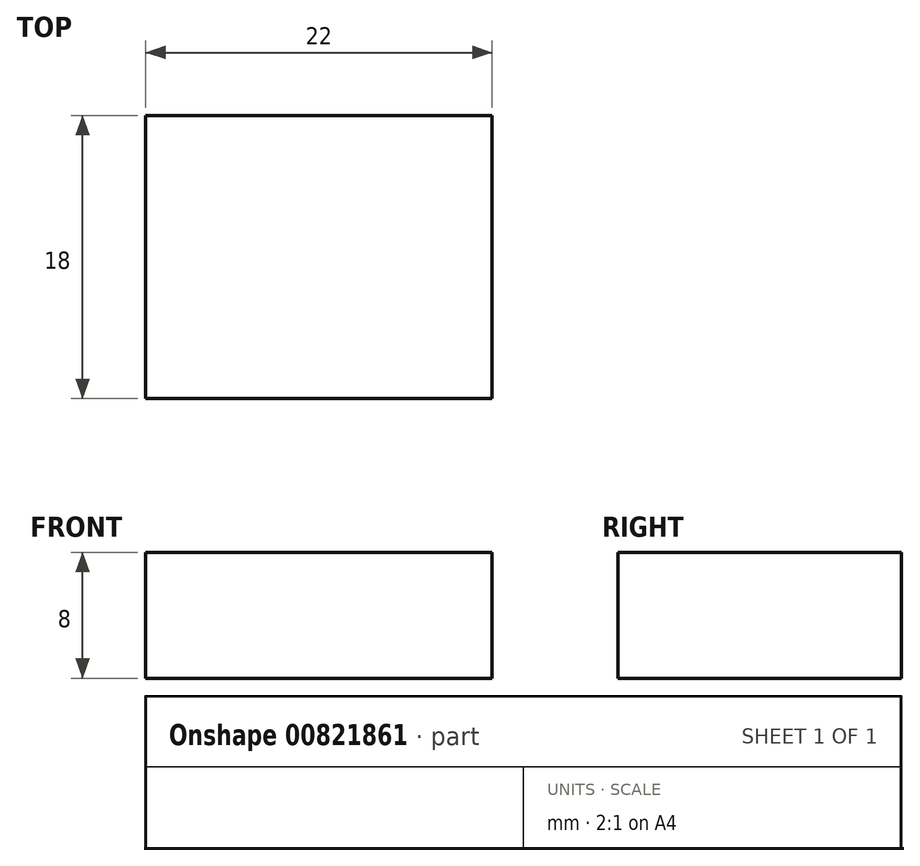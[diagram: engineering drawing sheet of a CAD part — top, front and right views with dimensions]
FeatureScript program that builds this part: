
annotation { "Feature Type Name" : "Feature", "Feature Type Description" : "" }
export const myFeature = defineFeature(function(context is Context, id is Id, definition is map)
    precondition{}
    {
        {
            var Q0;
            Q0=qCreatedBy(makeId("Right.planeOp"),FACE);
            var sketch = newSketch(context, id + "F0", { "sketchPlane" : qUnion([Q0])});
            skLineSegment(sketch, "E0.bottom", {"start": v(-9, 4) * mm, "end": v(9, 4) * mm});
            skLineSegment(sketch, "E0.top", {"start": v(-9, -4) * mm, "end": v(9, -4) * mm});
            skLineSegment(sketch, "E0.left", {"start": v(-9, 4) * mm, "end": v(-9, -4) * mm});
            skLineSegment(sketch, "E0.right", {"start": v(9, 4) * mm, "end": v(9, -4) * mm});
            skSolve(sketch);
        }
        {
            var Q0;
            Q0=makeQuery(id+"F0.imprint","IMPRINT",FACE,{"disambiguationData":[TD([[makeQuery(id+"F0.imprint","IMPRINT",EDGE,{"derivedFrom":sQuery(id+"F0.wireOp",EDGE,"E0.bottom")}),-1.0]])]});
            extrude(context, id + "F1", {"entities" : qUnion([Q0]), "depth" : 22 * mm, "offsetDistance" : 25 * mm});
        }
    });
